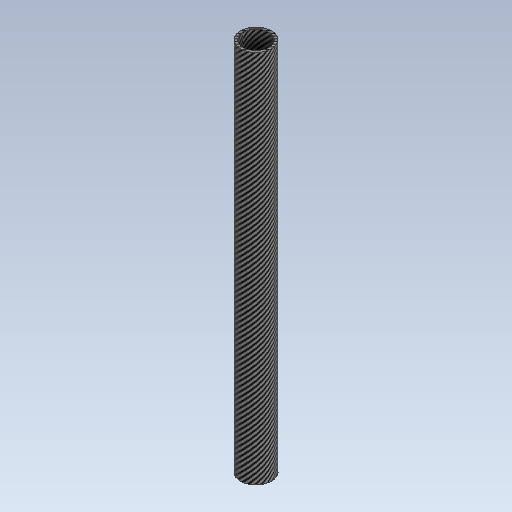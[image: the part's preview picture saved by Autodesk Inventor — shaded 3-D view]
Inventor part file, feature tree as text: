
AUTODESK INVENTOR PART (.ipt)
format: ipt  version: 2020 (Build 240168000, 168)  size: 126,976 bytes
history: native  units: mm
features: extrude x1, sketch x1
ambient origin geometry x8: Origin, YZ Plane, XZ Plane, XY Plane, X Axis, Y Axis, Z Axis, Center Point
bodies: Solid1 (feature_tree)
feature tree (2):
  extrude  "Extrusion1"  Depth=300.0mm
  sketch  "Sketch1"  dims[d0=25.0mm d1=21.0mm d2=300.0mm d3=0.0mm]
